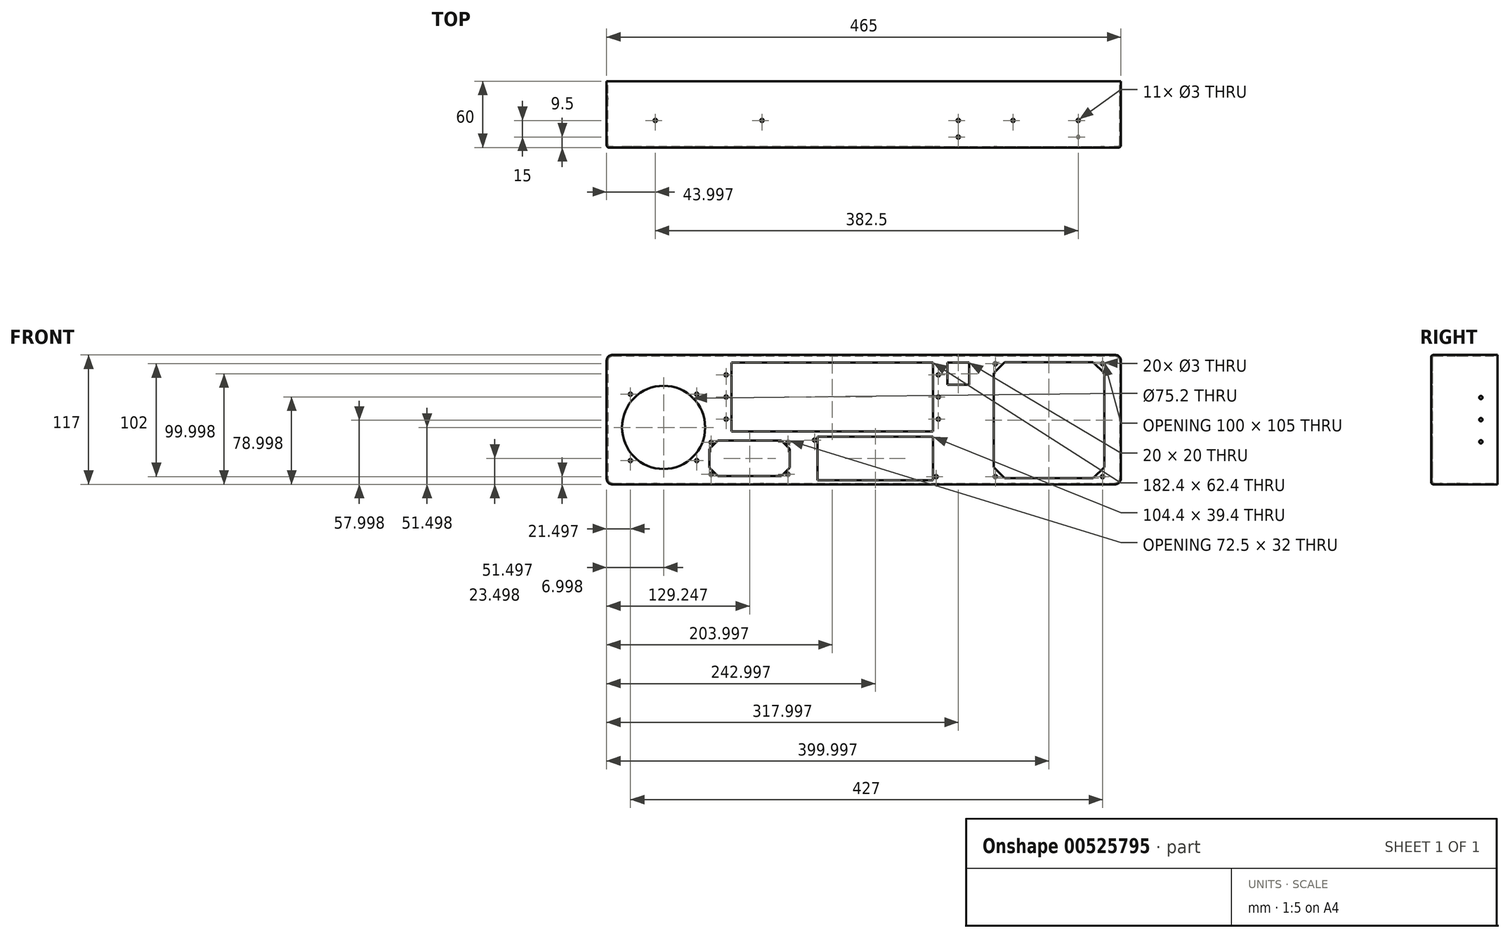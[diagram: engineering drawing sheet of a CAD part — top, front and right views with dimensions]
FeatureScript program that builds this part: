
annotation { "Feature Type Name" : "Feature", "Feature Type Description" : "" }
export const myFeature = defineFeature(function(context is Context, id is Id, definition is map)
    precondition{}
    {
        {
            var Q0;
            Q0=qCreatedBy(makeId("Front.planeOp"),FACE);
            var sketch = newSketch(context, id + "F0", { "sketchPlane" : qUnion([Q0])});
            skLineSegment(sketch, "E0.bottom", {"start": v(-245.15, 85.69) * mm, "end": v(219.85, 85.69) * mm});
            skLineSegment(sketch, "E0.top", {"start": v(-245.15, -31.31) * mm, "end": v(219.85, -31.31) * mm});
            skLineSegment(sketch, "E0.left", {"start": v(-245.15, 85.69) * mm, "end": v(-245.15, -31.31) * mm});
            skLineSegment(sketch, "E0.right", {"start": v(219.85, 85.69) * mm, "end": v(219.85, -31.31) * mm});
            skSolve(sketch);
        }
        {
            var Q0;
            Q0=qSketchRegion(id+"F0",true);
            var Q1;
            Q1=makeQuery(id+"F0.imprint","IMPRINT",FACE,{"disambiguationData":[TD([[makeQuery(id+"F0.imprint","IMPRINT",EDGE,{"derivedFrom":sQuery(id+"F0.wireOp",EDGE,"E0.bottom")}),-1.0]])]});
            extrude(context, id + "F1", {"entities" : qUnion([Q0, Q1]), "depth" : 60 * mm});
        }
        {
            var Q0;
            Q0=makeQuery(id+"F1.opExtrude","CAP_FACE",FACE,{"disambiguationData":[OSD([sQuery(id+"F0.wireOp",EDGE,"E0.bottom"),sQuery(id+"F0.wireOp",EDGE,"E0.top"),sQuery(id+"F0.wireOp",EDGE,"E0.left"),sQuery(id+"F0.wireOp",EDGE,"E0.right")])],"isStart":true});
            shell(context, id + "F2", {"entities" : qUnion([Q0]), "thickness" : 1 * mm});
        }
        {
            var Q0;
            Q0=makeQuery(id+"F1.opExtrude","CAP_FACE",FACE,{"disambiguationData":[OSD([sQuery(id+"F0.wireOp",EDGE,"E0.bottom"),sQuery(id+"F0.wireOp",EDGE,"E0.top"),sQuery(id+"F0.wireOp",EDGE,"E0.left"),sQuery(id+"F0.wireOp",EDGE,"E0.right")])],"isStart":false});
            var sketch = newSketch(context, id + "F3", { "sketchPlane" : qUnion([Q0])});
            skLineSegment(sketch, "E1.bottom", {"start": v(62.85, 78.69) * mm, "end": v(82.85, 78.69) * mm});
            skLineSegment(sketch, "E1.top", {"start": v(62.85, 58.69) * mm, "end": v(82.85, 58.69) * mm});
            skLineSegment(sketch, "E1.left", {"start": v(62.85, 78.69) * mm, "end": v(62.85, 58.69) * mm});
            skLineSegment(sketch, "E1.right", {"start": v(82.85, 78.69) * mm, "end": v(82.85, 58.69) * mm});
            skLineSegment(sketch, "E2.bottom", {"start": v(114.85, 79.19) * mm, "end": v(194.85, 79.19) * mm});
            skLineSegment(sketch, "E2.top", {"start": v(114.85, -25.81) * mm, "end": v(194.85, -25.81) * mm});
            skLineSegment(sketch, "E2.left", {"start": v(104.85, 69.19) * mm, "end": v(104.85, -15.81) * mm});
            skLineSegment(sketch, "E2.right", {"start": v(204.85, 69.19) * mm, "end": v(204.85, -15.81) * mm});
            skCircle(sketch, "E3", {"center": v(54.85, 67.69) * mm, "radius": 1.5 * mm});
            skCircle(sketch, "E4", {"center": v(54.85, 47.69) * mm, "radius": 1.5 * mm});
            skCircle(sketch, "E5", {"center": v(54.85, 27.69) * mm, "radius": 1.5 * mm});
            skCircle(sketch, "E6", {"center": v(106.35, 77.69) * mm, "radius": 1.5 * mm});
            skLineSegment(sketch, "E7", {"start": v(104.85, 69.19) * mm, "end": v(114.85, 79.19) * mm});
            skLineSegment(sketch, "E8.bottom", {"start": v(-144.65, 8.19) * mm, "end": v(-87.15, 8.19) * mm});
            skLineSegment(sketch, "E8.top", {"start": v(-144.65, -23.81) * mm, "end": v(-87.15, -23.81) * mm});
            skLineSegment(sketch, "E8.left", {"start": v(-152.15, 0.69) * mm, "end": v(-152.15, -16.31) * mm});
            skLineSegment(sketch, "E8.right", {"start": v(-79.65, 0.69) * mm, "end": v(-79.65, -16.31) * mm});
            skLineSegment(sketch, "E9", {"start": v(104.85, -15.81) * mm, "end": v(114.85, -25.81) * mm});
            skLineSegment(sketch, "E10", {"start": v(194.85, -25.81) * mm, "end": v(204.85, -15.81) * mm});
            skLineSegment(sketch, "E11", {"start": v(194.85, 79.19) * mm, "end": v(204.85, 69.19) * mm});
            skCircle(sketch, "E12", {"center": v(-193.65, 20.19) * mm, "radius": 37.6 * mm});
            skLineSegment(sketch, "E13", {"start": v(-152.15, 0.69) * mm, "end": v(-144.65, 8.19) * mm});
            skLineSegment(sketch, "E14", {"start": v(-87.15, 8.19) * mm, "end": v(-79.65, 0.69) * mm});
            skLineSegment(sketch, "E15", {"start": v(-79.65, -16.31) * mm, "end": v(-87.15, -23.81) * mm});
            skLineSegment(sketch, "E16", {"start": v(-152.15, -16.31) * mm, "end": v(-144.65, -23.81) * mm});
            skCircle(sketch, "E17", {"center": v(-137.15, 67.69) * mm, "radius": 1.5 * mm});
            skCircle(sketch, "E18", {"center": v(-137.15, 47.69) * mm, "radius": 1.5 * mm});
            skCircle(sketch, "E19", {"center": v(-137.15, 27.69) * mm, "radius": 1.5 * mm});
            skCircle(sketch, "E20", {"center": v(-223.65, 50.19) * mm, "radius": 1.5 * mm});
            skCircle(sketch, "E21", {"center": v(-223.65, -9.81) * mm, "radius": 1.5 * mm});
            skCircle(sketch, "E22", {"center": v(-163.65, -9.81) * mm, "radius": 1.5 * mm});
            skCircle(sketch, "E23", {"center": v(-163.65, 50.19) * mm, "radius": 1.5 * mm});
            skCircle(sketch, "E24", {"center": v(-57.15, 8.69) * mm, "radius": 1.5 * mm});
            skCircle(sketch, "E25", {"center": v(52.85, -24.31) * mm, "radius": 1.5 * mm});
            skLineSegment(sketch, "E26.bottom", {"start": v(-163.65, -9.81) * mm, "end": v(-223.65, -9.81) * mm, "construction": true});
            skLineSegment(sketch, "E26.top", {"start": v(-163.65, 50.19) * mm, "end": v(-223.65, 50.19) * mm, "construction": true});
            skLineSegment(sketch, "E26.left", {"start": v(-163.65, -9.81) * mm, "end": v(-163.65, 50.19) * mm, "construction": true});
            skLineSegment(sketch, "E26.right", {"start": v(-223.65, -9.81) * mm, "end": v(-223.65, 50.19) * mm, "construction": true});
            skCircle(sketch, "E27", {"center": v(-150.65, 6.69) * mm, "radius": 1.5 * mm});
            skCircle(sketch, "E28", {"center": v(-81.15, 6.69) * mm, "radius": 1.5 * mm});
            skCircle(sketch, "E29", {"center": v(-150.65, -22.31) * mm, "radius": 1.5 * mm});
            skCircle(sketch, "E30", {"center": v(-81.15, -22.31) * mm, "radius": 1.5 * mm});
            skCircle(sketch, "E31", {"center": v(203.35, 77.69) * mm, "radius": 1.5 * mm});
            skCircle(sketch, "E32", {"center": v(106.35, -24.31) * mm, "radius": 1.5 * mm});
            skCircle(sketch, "E33", {"center": v(203.35, -24.31) * mm, "radius": 1.5 * mm});
            skLineSegment(sketch, "E34.bottom", {"start": v(50.05, 16.49) * mm, "end": v(-132.35, 16.49) * mm});
            skLineSegment(sketch, "E34.top", {"start": v(50.05, 78.89) * mm, "end": v(-132.35, 78.89) * mm});
            skLineSegment(sketch, "E34.left", {"start": v(50.05, 16.49) * mm, "end": v(50.05, 78.89) * mm});
            skLineSegment(sketch, "E34.right", {"start": v(-132.35, 16.49) * mm, "end": v(-132.35, 78.89) * mm});
            skPoint(sketch, "E34.middle", {"position": v(-41.15, 47.69) * mm});
            skLineSegment(sketch, "E35.bottom", {"start": v(50.05, -27.51) * mm, "end": v(-54.35, -27.51) * mm});
            skLineSegment(sketch, "E35.top", {"start": v(50.05, 11.89) * mm, "end": v(-54.35, 11.89) * mm});
            skLineSegment(sketch, "E35.left", {"start": v(50.05, -27.51) * mm, "end": v(50.05, 11.89) * mm});
            skLineSegment(sketch, "E35.right", {"start": v(-54.35, -27.51) * mm, "end": v(-54.35, 11.89) * mm});
            skPoint(sketch, "E35.middle", {"position": v(-2.15, -7.81) * mm});
            skSolve(sketch);
        }
        {
            var Q0;
            Q0=qSketchRegion(id+"F3",true);
            extrude(context, id + "F4", {"entities" : qUnion([Q0]), "operationType" : NewBodyOperationType.REMOVE, "oppositeDirection" : true, "depth" : 25 * mm});
        }
        {
            var Q0;
            Q0=makeQuery(id+"F1.opExtrude","SWEPT_FACE",FACE,{"disambiguationData":[OSD([sQuery(id+"F0.wireOp",EDGE,"E0.left")])]});
            var sketch = newSketch(context, id + "F5", { "sketchPlane" : qUnion([Q0])});
            skCircle(sketch, "E36", {"center": v(15, 47.19) * mm, "radius": 1.5 * mm});
            skCircle(sketch, "E37", {"center": v(15, 7.19) * mm, "radius": 1.5 * mm});
            skLineSegment(sketch, "E38", {"start": v(-16.01, 27.19) * mm, "end": v(37.35, 27.19) * mm, "construction": true});
            skPoint(sketch, "E39.middle.positionSnap0", {"position": v(0, 27.19) * mm});
            skPoint(sketch, "E39.centerSnap0", {"position": v(0, 27.19) * mm});
            skCircle(sketch, "E40", {"center": v(15, 27.19) * mm, "radius": 1.5 * mm});
            skSolve(sketch);
        }
        {
            var Q0;
            Q0=qSketchRegion(id+"F5",true);
            extrude(context, id + "F6", {"entities" : qUnion([Q0]), "operationType" : NewBodyOperationType.REMOVE, "oppositeDirection" : true, "depth" : 500 * mm});
        }
        {
            var Q0;
            Q0=makeQuery(id+"F1.opExtrude","SWEPT_FACE",FACE,{"disambiguationData":[OSD([sQuery(id+"F0.wireOp",EDGE,"E0.bottom")])]});
            var sketch = newSketch(context, id + "F7", { "sketchPlane" : qUnion([Q0])});
            skCircle(sketch, "E41", {"center": v(-201.15, -35.5) * mm, "radius": 1.5 * mm});
            skCircle(sketch, "E42", {"center": v(-104.65, -35.5) * mm, "radius": 1.5 * mm});
            skCircle(sketch, "E43", {"center": v(122.35, -35.5) * mm, "radius": 1.5 * mm});
            skCircle(sketch, "E44", {"center": v(181.35, -35.5) * mm, "radius": 1.5 * mm});
            skCircle(sketch, "E45", {"center": v(72.85, -35.5) * mm, "radius": 1.5 * mm});
            skCircle(sketch, "E46", {"center": v(72.85, -50.5) * mm, "radius": 1.5 * mm});
            skCircle(sketch, "E47", {"center": v(181.35, -50.5) * mm, "radius": 1.5 * mm, "construction": true});
            skSolve(sketch);
        }
        {
            var Q0;
            Q0=makeQuery(id+"F7.imprint","IMPRINT",FACE,{"disambiguationData":[TD([[makeQuery(id+"F7.imprint","IMPRINT",EDGE,{"derivedFrom":sQuery(id+"F7.wireOp",EDGE,"E41")}),1.0]])]});
            var Q1;
            Q1=makeQuery(id+"F7.imprint","IMPRINT",FACE,{"disambiguationData":[TD([[makeQuery(id+"F7.imprint","IMPRINT",EDGE,{"derivedFrom":sQuery(id+"F7.wireOp",EDGE,"E42")}),1.0]])]});
            var Q2;
            Q2=makeQuery(id+"F7.imprint","IMPRINT",FACE,{"disambiguationData":[TD([[makeQuery(id+"F7.imprint","IMPRINT",EDGE,{"derivedFrom":sQuery(id+"F7.wireOp",EDGE,"E43")}),1.0]])]});
            var Q3;
            Q3=makeQuery(id+"F7.imprint","IMPRINT",FACE,{"disambiguationData":[TD([[makeQuery(id+"F7.imprint","IMPRINT",EDGE,{"derivedFrom":sQuery(id+"F7.wireOp",EDGE,"E44")}),1.0]])]});
            var Q4;
            Q4=makeQuery(id+"F7.imprint","IMPRINT",FACE,{"disambiguationData":[TD([[makeQuery(id+"F7.imprint","IMPRINT",EDGE,{"derivedFrom":sQuery(id+"F7.wireOp",EDGE,"E47")}),1.0]])]});
            extrude(context, id + "F8", {"entities" : qUnion([Q0, Q1, Q2, Q3, Q4]), "operationType" : NewBodyOperationType.REMOVE, "endBound" : BoundingType.THROUGH_ALL, "oppositeDirection" : true, "depth" : 117 * mm});
        }
        {
            var Q0;
            Q0=makeQuery(id+"F7.imprint","IMPRINT",FACE,{"disambiguationData":[TD([[makeQuery(id+"F7.imprint","IMPRINT",EDGE,{"derivedFrom":sQuery(id+"F7.wireOp",EDGE,"E45")}),1.0]])]});
            var Q1;
            Q1=makeQuery(id+"F7.imprint","IMPRINT",FACE,{"disambiguationData":[TD([[makeQuery(id+"F7.imprint","IMPRINT",EDGE,{"derivedFrom":sQuery(id+"F7.wireOp",EDGE,"E46")}),1.0]])]});
            extrude(context, id + "F9", {"entities" : qUnion([Q0, Q1]), "operationType" : NewBodyOperationType.REMOVE, "oppositeDirection" : true, "depth" : 2 * mm});
        }
        {
            var Q0;
            Q0=makeQuery(id+"F1.opExtrude","SWEPT_FACE",FACE,{"disambiguationData":[OSD([sQuery(id+"F0.wireOp",EDGE,"E0.top")])]});
            var sketch = newSketch(context, id + "F10", { "sketchPlane" : qUnion([Q0])});
            skCircle(sketch, "E48", {"center": v(181.35, 50.5) * mm, "radius": 1.5 * mm});
            skCircle(sketch, "E49.0", {"center": v(181.35, 35.5) * mm, "radius": 1.5 * mm, "construction": true});
            skSolve(sketch);
        }
        {
            var Q0;
            Q0=qSketchRegion(id+"F10",true);
            extrude(context, id + "F11", {"entities" : qUnion([Q0]), "operationType" : NewBodyOperationType.REMOVE, "oppositeDirection" : true, "depth" : 2 * mm});
        }
        {
            var Q0;
            Q0=makeQuery(id+"F1.opExtrude","SWEPT_EDGE",EDGE,{"disambiguationData":[OSD([sQuery(id+"F0.wireOp",EDGE,"E0.bottom"),sQuery(id+"F0.wireOp",EDGE,"E0.left")])]});
            var Q1;
            Q1=makeQuery(id+"F1.opExtrude","SWEPT_EDGE",EDGE,{"disambiguationData":[OSD([sQuery(id+"F0.wireOp",EDGE,"E0.bottom"),sQuery(id+"F0.wireOp",EDGE,"E0.right")])]});
            var Q2;
            Q2=makeQuery(id+"F1.opExtrude","SWEPT_EDGE",EDGE,{"disambiguationData":[OSD([sQuery(id+"F0.wireOp",EDGE,"E0.top"),sQuery(id+"F0.wireOp",EDGE,"E0.right")])]});
            var Q3;
            Q3=makeQuery(id+"F1.opExtrude","SWEPT_EDGE",EDGE,{"disambiguationData":[OSD([sQuery(id+"F0.wireOp",EDGE,"E0.top"),sQuery(id+"F0.wireOp",EDGE,"E0.left")])]});
            var Q4;
            Q4=makeQuery(id+"F2.opShell","OFFSET_EDGE",EDGE,{"disambiguationData":[OSD([sQuery(id+"F0.wireOp",EDGE,"E0.bottom"),sQuery(id+"F0.wireOp",EDGE,"E0.left")])]});
            var Q5;
            Q5=makeQuery(id+"F2.opShell","OFFSET_EDGE",EDGE,{"disambiguationData":[OSD([sQuery(id+"F0.wireOp",EDGE,"E0.top"),sQuery(id+"F0.wireOp",EDGE,"E0.left")])]});
            var Q6;
            Q6=makeQuery(id+"F2.opShell","OFFSET_EDGE",EDGE,{"disambiguationData":[OSD([sQuery(id+"F0.wireOp",EDGE,"E0.top"),sQuery(id+"F0.wireOp",EDGE,"E0.right")])]});
            var Q7;
            Q7=makeQuery(id+"F2.opShell","OFFSET_EDGE",EDGE,{"disambiguationData":[OSD([sQuery(id+"F0.wireOp",EDGE,"E0.bottom"),sQuery(id+"F0.wireOp",EDGE,"E0.right")])]});
            fillet(context, id + "F12", {"entities" : qUnion([Q0, Q1, Q2, Q3, Q4, Q5, Q6, Q7]), "radius" : 5 * mm, "tangentPropagation" : true, "allowEdgeOverflow" : false});
        }
        {
            var Q0;
            {var subQ0=sQuery(id+"F0.wireOp",EDGE,"E0.right");var subQ1=sQuery(id+"F0.wireOp",EDGE,"E0.bottom");Q0=makeQuery(id+"F12.opFillet","BLEND_EDGE",EDGE,{"blendedFrom":[makeQuery(id+"F1.opExtrude","SWEPT_EDGE",EDGE,{"disambiguationData":[OSD([subQ1,subQ0])]}),makeQuery(id+"F1.opExtrude","CAP_FACE",FACE,{"disambiguationData":[OSD([subQ1,sQuery(id+"F0.wireOp",EDGE,"E0.top"),sQuery(id+"F0.wireOp",EDGE,"E0.left"),subQ0])],"isStart":false})],"blendedInto":[makeQuery(id+"F1.opExtrude","CAP_FACE",FACE,{"disambiguationData":[OSD([subQ1,sQuery(id+"F0.wireOp",EDGE,"E0.top"),sQuery(id+"F0.wireOp",EDGE,"E0.left"),subQ0])],"isStart":false})]});}
            var Q1;
            {var subQ0=sQuery(id+"F0.wireOp",EDGE,"E0.bottom");Q1=makeQuery(id+"F2.opShell","OFFSET_EDGE",EDGE,{"disambiguationData":[OSD([subQ0]),TDD([makeQuery(id+"F1.opExtrude","CAP_EDGE",EDGE,{"disambiguationData":[OSD([subQ0])],"isStart":false})])]});}
            fillet(context, id + "F13", {"entities" : qUnion([Q0, Q1]), "radius" : 2 * mm, "tangentPropagation" : true, "allowEdgeOverflow" : false});
        }
    });
